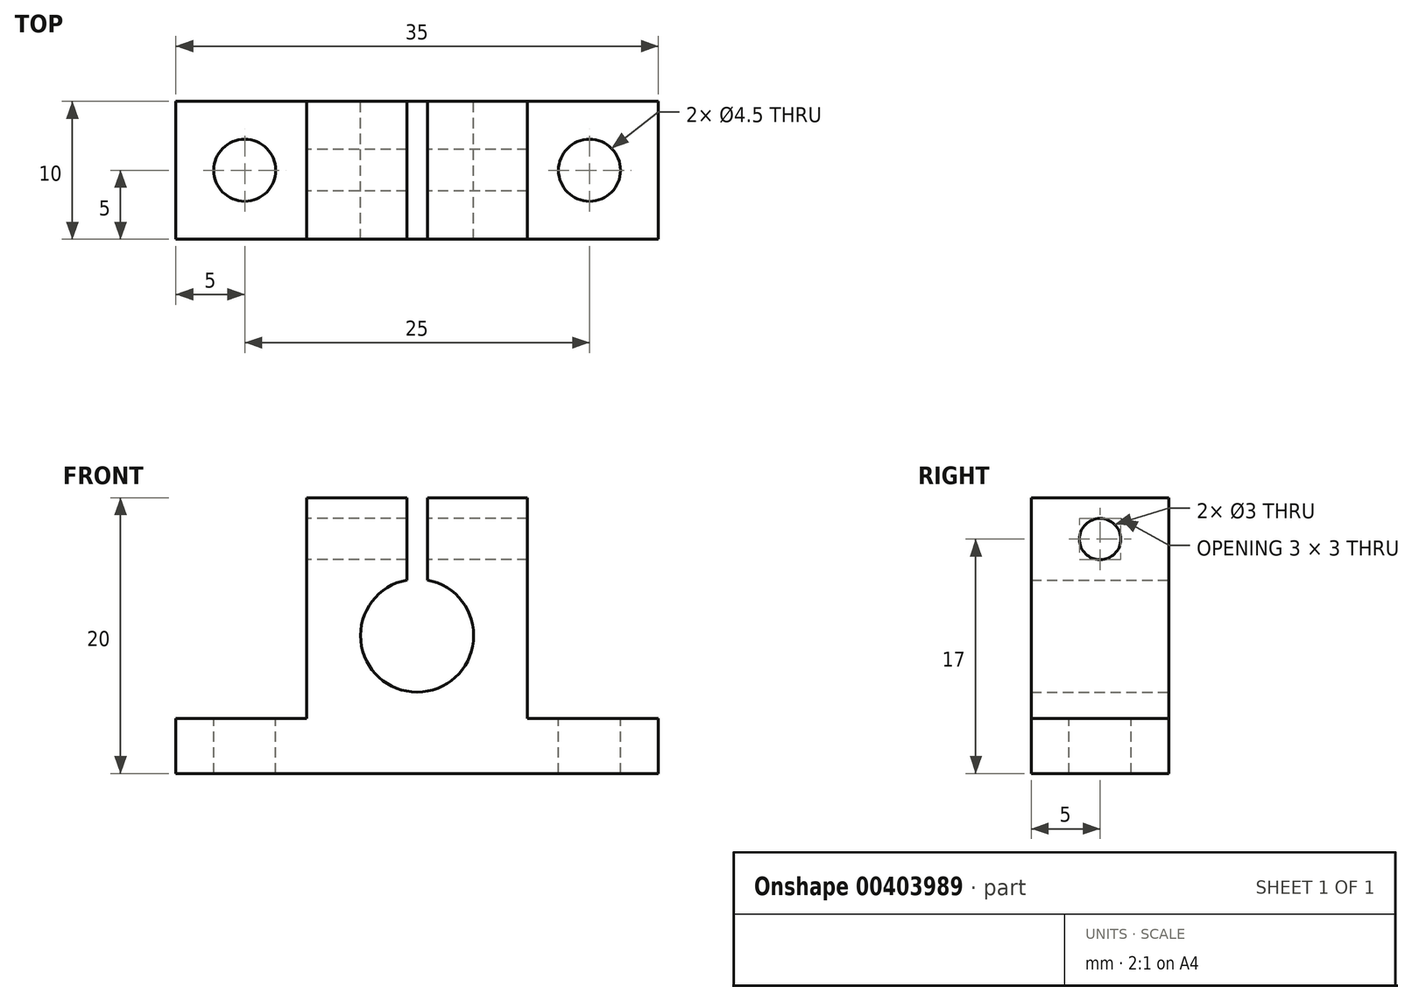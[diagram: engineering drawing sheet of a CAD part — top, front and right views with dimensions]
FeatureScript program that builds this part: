
annotation { "Feature Type Name" : "Feature", "Feature Type Description" : "" }
export const myFeature = defineFeature(function(context is Context, id is Id, definition is map)
    precondition{}
    {
        {
            var Q0;
            Q0=qCreatedBy(makeId("Front.planeOp"),FACE);
            var sketch = newSketch(context, id + "F0", { "sketchPlane" : qUnion([Q0])});
            skLineSegment(sketch, "E0.bottom", {"start": v(-8, 0) * mm, "end": v(8, 0) * mm});
            skLineSegment(sketch, "E0.top", {"start": v(-8, 20) * mm, "end": v(-0.75, 20) * mm});
            skLineSegment(sketch, "E0.left", {"start": v(-8, 4) * mm, "end": v(-8, 20) * mm});
            skLineSegment(sketch, "E0.right", {"start": v(8, 4) * mm, "end": v(8, 20) * mm});
            skArc(sketch, "E1", {"start": v(-0.75, 14.03) * mm, "mid": v(0, 5.9) * mm, "end": v(0.75, 14.03) * mm});
            skLineSegment(sketch, "E2", {"start": v(-8, 0) * mm, "end": v(-17.5, 0) * mm});
            skLineSegment(sketch, "E3", {"start": v(-17.5, 0) * mm, "end": v(-17.5, 4) * mm});
            skLineSegment(sketch, "E4", {"start": v(-17.5, 4) * mm, "end": v(-8, 4) * mm});
            skLineSegment(sketch, "E5", {"start": v(8, 0) * mm, "end": v(17.5, 0) * mm});
            skLineSegment(sketch, "E6", {"start": v(17.5, 0) * mm, "end": v(17.5, 4) * mm});
            skLineSegment(sketch, "E7", {"start": v(17.5, 4) * mm, "end": v(8, 4) * mm});
            skLineSegment(sketch, "E8", {"start": v(-0.75, 20) * mm, "end": v(-0.75, 14.03) * mm});
            skLineSegment(sketch, "E9", {"start": v(0.75, 20) * mm, "end": v(0.75, 14.03) * mm});
            skLineSegment(sketch, "E10.trimOffspring", {"start": v(0.75, 20) * mm, "end": v(8, 20) * mm});
            skSolve(sketch);
        }
        {
            var Q0;
            Q0=makeQuery(id+"F0.imprint","IMPRINT",FACE,{"disambiguationData":[TD([[makeQuery(id+"F0.imprint","IMPRINT",EDGE,{"derivedFrom":sQuery(id+"F0.wireOp",EDGE,"E0.bottom")}),1.0]])]});
            extrude(context, id + "F1", {"entities" : qUnion([Q0]), "depth" : 10 * mm});
        }
        {
            var Q0;
            Q0=makeQuery(id+"F1.opExtrude","SWEPT_FACE",FACE,{"disambiguationData":[OSD([sQuery(id+"F0.wireOp",EDGE,"E4")])]});
            var sketch = newSketch(context, id + "F2", { "sketchPlane" : qUnion([Q0])});
            skLineSegment(sketch, "E11", {"start": v(-17.5, -5) * mm, "end": v(17.5, -5) * mm, "construction": true});
            skPoint(sketch, "E12", {"position": v(-12.5, -5) * mm});
            skPoint(sketch, "E13", {"position": v(12.5, -5) * mm});
            skSolve(sketch);
        }
        {
            var Q0;
            Q0=sQuery(id+"F2.wireOp",VERTEX,"E12");
            var Q1;
            Q1=sQuery(id+"F2.wireOp",VERTEX,"E13");
            var Q2;
            Q2=makeQuery(id+"F1.opExtrude","SWEPT_BODY",BODY,{"disambiguationData":[OSD([sQuery(id+"F0.wireOp",EDGE,"E0.bottom"),sQuery(id+"F0.wireOp",EDGE,"E0.top"),sQuery(id+"F0.wireOp",EDGE,"E0.left"),sQuery(id+"F0.wireOp",EDGE,"E0.right"),sQuery(id+"F0.wireOp",EDGE,"E1"),sQuery(id+"F0.wireOp",EDGE,"E2"),sQuery(id+"F0.wireOp",EDGE,"E3"),sQuery(id+"F0.wireOp",EDGE,"E4"),sQuery(id+"F0.wireOp",EDGE,"E5"),sQuery(id+"F0.wireOp",EDGE,"E6"),sQuery(id+"F0.wireOp",EDGE,"E7"),sQuery(id+"F0.wireOp",EDGE,"E8"),sQuery(id+"F0.wireOp",EDGE,"E9"),sQuery(id+"F0.wireOp",EDGE,"E10.trimOffspring")])]});
            hole(context, id + "F3", {"style" : HoleStyle.SIMPLE, "endStyle" : HoleEndStyle.THROUGH, "holeDiameter" : 4.5 * mm, "isTappedThrough" : true, "tappedDepth" : 12 * mm, "tapClearance" : 3, "locations" : qUnion([Q0, Q1]), "scope" : qUnion([Q2])});
        }
        {
            var Q0;
            Q0=makeQuery(id+"F1.opExtrude","SWEPT_FACE",FACE,{"disambiguationData":[OSD([sQuery(id+"F0.wireOp",EDGE,"E0.left")])]});
            var sketch = newSketch(context, id + "F4", { "sketchPlane" : qUnion([Q0])});
            skLineSegment(sketch, "E14", {"start": v(5, 20) * mm, "end": v(5, 0) * mm});
            skPoint(sketch, "E15", {"position": v(5, 17) * mm});
            skSolve(sketch);
        }
        {
            var Q0;
            Q0=sQuery(id+"F4.wireOp",VERTEX,"E15");
            var Q1;
            Q1=makeQuery(id+"F1.opExtrude","SWEPT_BODY",BODY,{"disambiguationData":[OSD([sQuery(id+"F0.wireOp",EDGE,"E0.bottom"),sQuery(id+"F0.wireOp",EDGE,"E0.top"),sQuery(id+"F0.wireOp",EDGE,"E0.left"),sQuery(id+"F0.wireOp",EDGE,"E0.right"),sQuery(id+"F0.wireOp",EDGE,"E1"),sQuery(id+"F0.wireOp",EDGE,"E2"),sQuery(id+"F0.wireOp",EDGE,"E3"),sQuery(id+"F0.wireOp",EDGE,"E4"),sQuery(id+"F0.wireOp",EDGE,"E5"),sQuery(id+"F0.wireOp",EDGE,"E6"),sQuery(id+"F0.wireOp",EDGE,"E7"),sQuery(id+"F0.wireOp",EDGE,"E8"),sQuery(id+"F0.wireOp",EDGE,"E9"),sQuery(id+"F0.wireOp",EDGE,"E10.trimOffspring")])]});
            hole(context, id + "F5", {"style" : HoleStyle.SIMPLE, "endStyle" : HoleEndStyle.THROUGH, "holeDiameter" : 3 * mm, "isTappedThrough" : true, "tappedDepth" : 12 * mm, "tapClearance" : 3, "locations" : qUnion([Q0]), "scope" : qUnion([Q1])});
        }
    });
